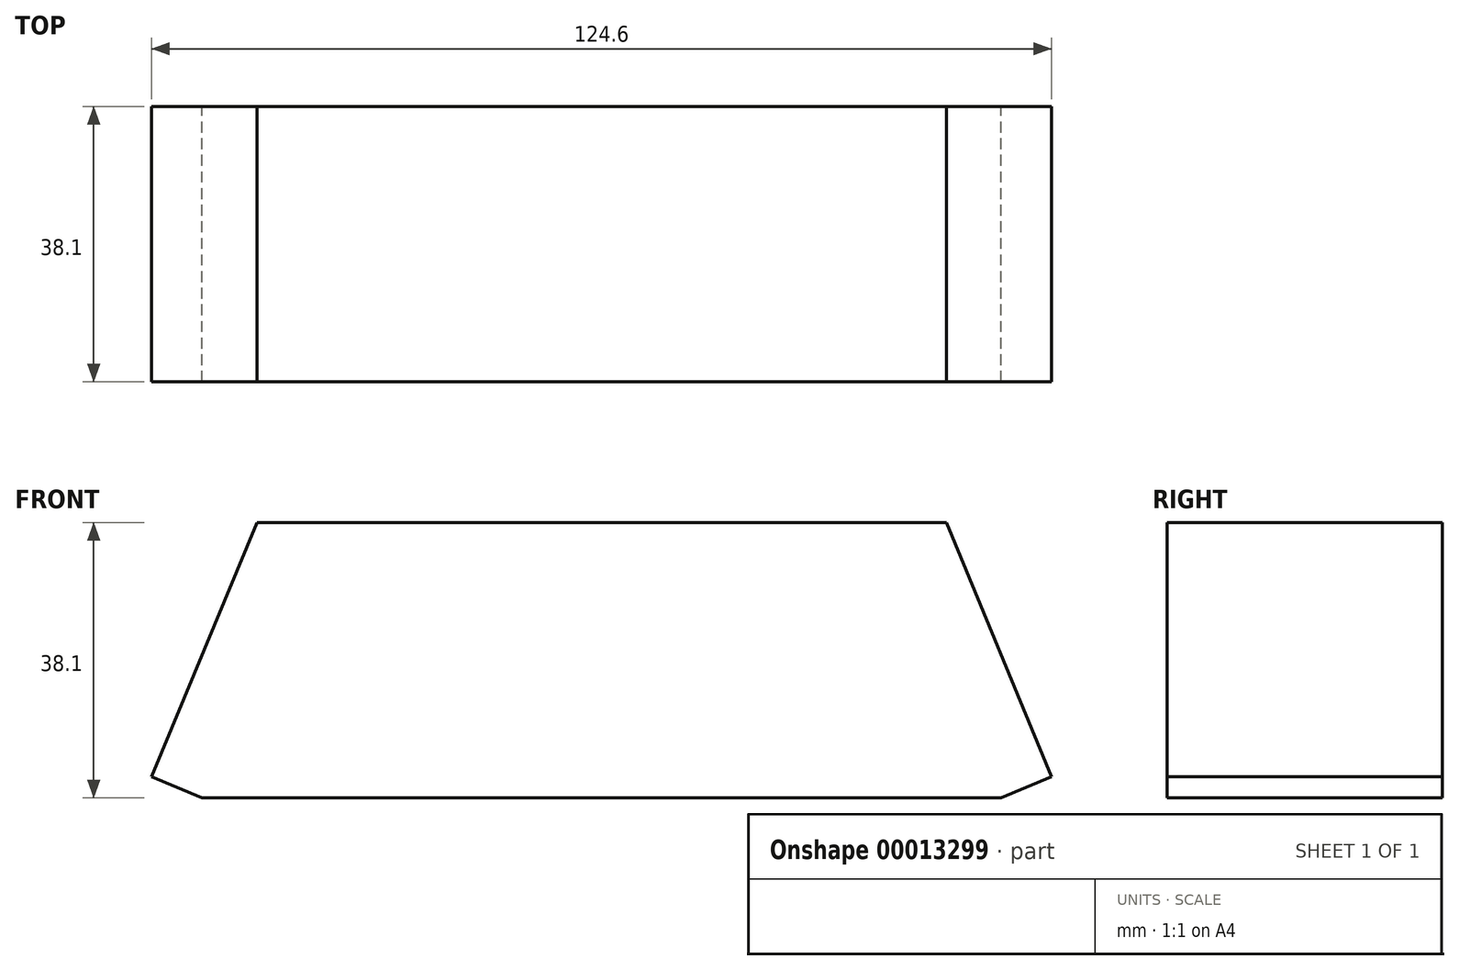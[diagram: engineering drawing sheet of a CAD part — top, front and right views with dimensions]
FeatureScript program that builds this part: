
annotation { "Feature Type Name" : "Feature", "Feature Type Description" : "" }
export const myFeature = defineFeature(function(context is Context, id is Id, definition is map)
    precondition{}
    {
        {
            var Q0;
            Q0=qCreatedBy(makeId("Front.planeOp"),FACE);
            var sketch = newSketch(context, id + "F0", { "sketchPlane" : qUnion([Q0])});
            skLineSegment(sketch, "E0", {"start": v(-63.5, 0) * mm, "end": v(0, 0) * mm});
            skLineSegment(sketch, "E1", {"start": v(0, 0) * mm, "end": v(63.5, 0) * mm});
            skLineSegment(sketch, "E2", {"start": v(63.5, 0) * mm, "end": v(47.72, 38.1) * mm});
            skLineSegment(sketch, "E3", {"start": v(47.72, 38.1) * mm, "end": v(-47.72, 38.1) * mm});
            skLineSegment(sketch, "E4", {"start": v(-47.72, 38.1) * mm, "end": v(-63.5, 0) * mm});
            skLineSegment(sketch, "E5", {"start": v(-62.3, 2.9) * mm, "end": v(-55.3, 0) * mm});
            skLineSegment(sketch, "E6", {"start": v(62.3, 2.9) * mm, "end": v(55.3, 0) * mm});
            skSolve(sketch);
        }
        {
            var Q0;
            {var subQ3=sQuery(id+"F0.wireOp",EDGE,"E3");Q0=makeQuery(id+"F0.imprint","IMPRINT",FACE,{"disambiguationData":[TD([[makeQuery(id+"F0.imprint","IMPRINT",EDGE,{"derivedFrom":subQ3}),1.0]])]});}
            var Q1;
            Q1=sQuery(id+"F0.wireOp",EDGE,"E4");
            var Q2;
            Q2=sQuery(id+"F0.wireOp",EDGE,"E0");
            var Q3;
            Q3=sQuery(id+"F0.wireOp",EDGE,"E1");
            var Q4;
            Q4=sQuery(id+"F0.wireOp",EDGE,"E2");
            var Q5;
            Q5=sQuery(id+"F0.wireOp",EDGE,"E3");
            extrude(context, id + "F1", {"entities" : qUnion([Q0]), "surfaceEntities" : qUnion([Q1, Q2, Q3, Q4, Q5]), "endBound" : BoundingType.SYMMETRIC, "depth" : 38.1 * mm});
        }
    });
